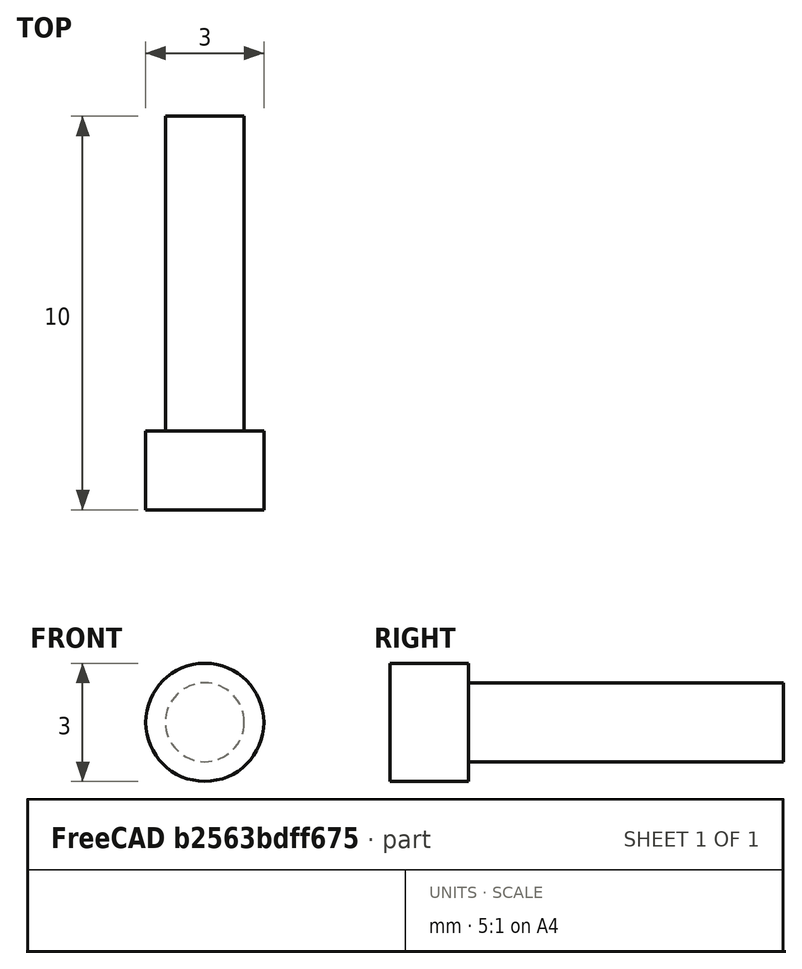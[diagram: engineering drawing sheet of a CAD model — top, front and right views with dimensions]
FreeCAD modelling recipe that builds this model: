
FCSTD DOCUMENT  (FreeCAD 1.0R39319 (Git))
Label: visM2L8
License: All rights reserved
LicenseURL: https://en.wikipedia.org/wiki/All_rights_reserved
objects: Sketcher::SketchObject×1, PartDesign::Revolution×1, PartDesign::Body×1
note: 6 computed .brp shape members not serialized (recipe doc carries the construction recipe); baked Part::Feature solids carry a one-line shape summary decoded from their .brp

FEATURE [Sketcher::SketchObject] Sketch
  ArcFitTolerance = 1e-06
  AttachmentSupport = -> [YZ_Plane]
  FullyConstrained = true
  MakeInternals = false
  MapMode = 5
  Placement = pos=(0,0,0) rot=(0.57735,0.57735,0.57735;2.0944rad)
  sketch-geometry (6):
    g0: LineSegment StartX=-2 StartY=0 StartZ=0 EndX=-2 EndY=1.5 EndZ=0
    g1: LineSegment StartX=-2 StartY=1.5 StartZ=0 EndX=-4.574e-13 EndY=1.5 EndZ=0
    g2: LineSegment StartX=-4.574e-13 StartY=1.5 StartZ=0 EndX=0 EndY=1 EndZ=0
    g3: LineSegment StartX=0 StartY=1 StartZ=0 EndX=8 EndY=1 EndZ=0
    g4: LineSegment StartX=8 StartY=0 StartZ=0 EndX=8 EndY=1 EndZ=0
    g5: LineSegment StartX=-2 StartY=0 StartZ=0 EndX=8 EndY=0 EndZ=0
  constraints (18):
    c: PointOnObject(g0,g-1)
    c: Vertical(g0)
    c: Coincident(g1,g0)
    c: PointOnObject(g1,g-2)
    c: Horizontal(g1)
    c: Coincident(g2,g1)
    c: PointOnObject(g2,g-2)
    c: Coincident(g3,g2)
    c: Horizontal(g3)
    c: PointOnObject(g4,g-1)
    c: Coincident(g5,g0)
    c: Coincident(g5,g4)
    c: Coincident(g4,g3)
    c: Perpendicular(g-1,g4)
    c: DistanceY(g0,g0) = 1.5
    c: DistanceX(g1,g1) = 2
    c: DistanceX(g3,g3) = 8
    c: DistanceY(g4,g4) = 1
FEATURE [PartDesign::Revolution] Revolution
  Angle = 360
  Angle2 = 60
  Axis = (1e-16,1,-1e-16)
  Base = (0,0,0)
  Placement = pos=(0,0,0) rot=(1,1,1;2.0944rad)
  Profile = -> Sketch
  ReferenceAxis = -> Y_Axis
  Refine = true
  Suppressed = false
  Type = 0
FEATURE [PartDesign::Body] Body  label="Corps"
  AllowCompound = false
  Group = -> [Sketch,Revolution]
  Origin = -> Origin
  Tip = -> Revolution
